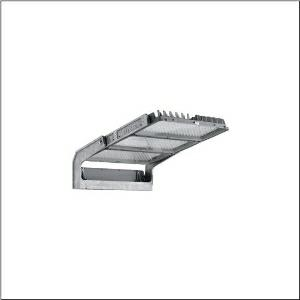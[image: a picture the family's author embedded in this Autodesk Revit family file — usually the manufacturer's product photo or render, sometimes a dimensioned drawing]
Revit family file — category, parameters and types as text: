
# Revit family: floodlight_fl_11_maxi_pro___rs12_5xa779228m01ab_5605
name_source: partatom
category: Lighting Fixtures
units: mm (PartAtom-declared; Revit-internal decimal feet)

## family parameters
Cut with Voids When Loaded = No
Host = Face
Light Source = No
Part Type = Normal
Room Calculation Point = No
Round Connector Dimension = Use Diameter
Shared = No

## types (1)
- --- (1 x LED, 179630 lm, 1571.1 W, 5700K)
    Apparent Load = 1571 VA
    CIE Flux Codes = 79 92 99 100 100
    Color Rendering = 80
    Color Temperature = 5700K
    Default Elevation = 1800 mm
    Description = Floodlight FL 11  maxi  pro floodlight; light control with lens of PMMA; cover panel of toughened safety glass, transparent; light distribution: RS12, rotationally symmetric direct distribution, LEDcolour temperature: 5700K, rated luminous flux: 179.630lm, colour rendering: CRI > 80, light colour: 857; luminous efficacy: 114lm/W; brightness control: DMX+RDM; with terminal, 6-pole, max. 2.5mm², mains connection: 220..240V/380..400V AC, 50/60Hz, surge voltage resistance: line to ground: 10kV, service life up to 100,000h L90. Typical operating time: 1000h per year, ECG replaceable separately, LED unit replaceable without ESD environment, dustproof LED module, dimming range 10..100%; 1571W floodlight with 3x LED unit of diecast aluminium, coated grey; length: 1.003mm / width: 651mm / height: 338mm; mounting bracket, of diecast aluminium, uncoated, natural, protection rating (complete): IP66; insulation class (complete): insulation class I (protective earthing); certification: CE, ENEC, VDE; ball protection: ball impact resistant, only for outdoor installations in the designated locations, permissible operating ambient temperature: -40..+55°C, permissible storage temperature: -40..+85°Cpackaging unit: 1 piece

Light Distribution: RS12
    Height = 320 mm
    Lamp = 1 x LED
    Lamp Light Flux = 179630 lm
    Lamp Power = 1571.1 W
    Lamp count = 1
    Length = 1002 mm
    Luminous efficacy = 114 lm/W
    Manufacturer = Siteco
    ModVariant = No
    Model = 5XA779228M01AB
    Mounting Place = Ceiling
    Mounting Type = Surface mounted
    Number of Poles = 1
    OnlyDefault = Yes
    Power Factor = 1
    Product Name = Floodlight FL 11 maxi pro | RS12
    Product group = floodlight | ceiling mounted
    ProductGroupID = 301
    Protection Class = Protection class I
    Protection Degree = IP 66
    RLX_Detail_Level = 1
    RLX_Emergency_Light_Flux = 0 lm
    RLX_Emergency_Type = 0
    RLX_Emergency_Type_DB = No
    RlxData = <blob elided: 40129 chars, md5=1476288b>
    Socket = socket
    Standby Power = 0 W
    System Light Flux = 179630 lm
    System Power = 1571 W
    Type Comments = factory setting: luminous flux: 100 % | dim-lin: 255 | 1060 mA
    Type Image = l_1356210.jpg
    URL = http://relux.com
    VarID = @adj_014007
    Voltage = 0 V
    Weight = 0.00 kg
    Width = 655 mm

## geometry (parser evidence)
native form markers: Blend x4, Sweep x11
no freeform markers — native parametric forms only
